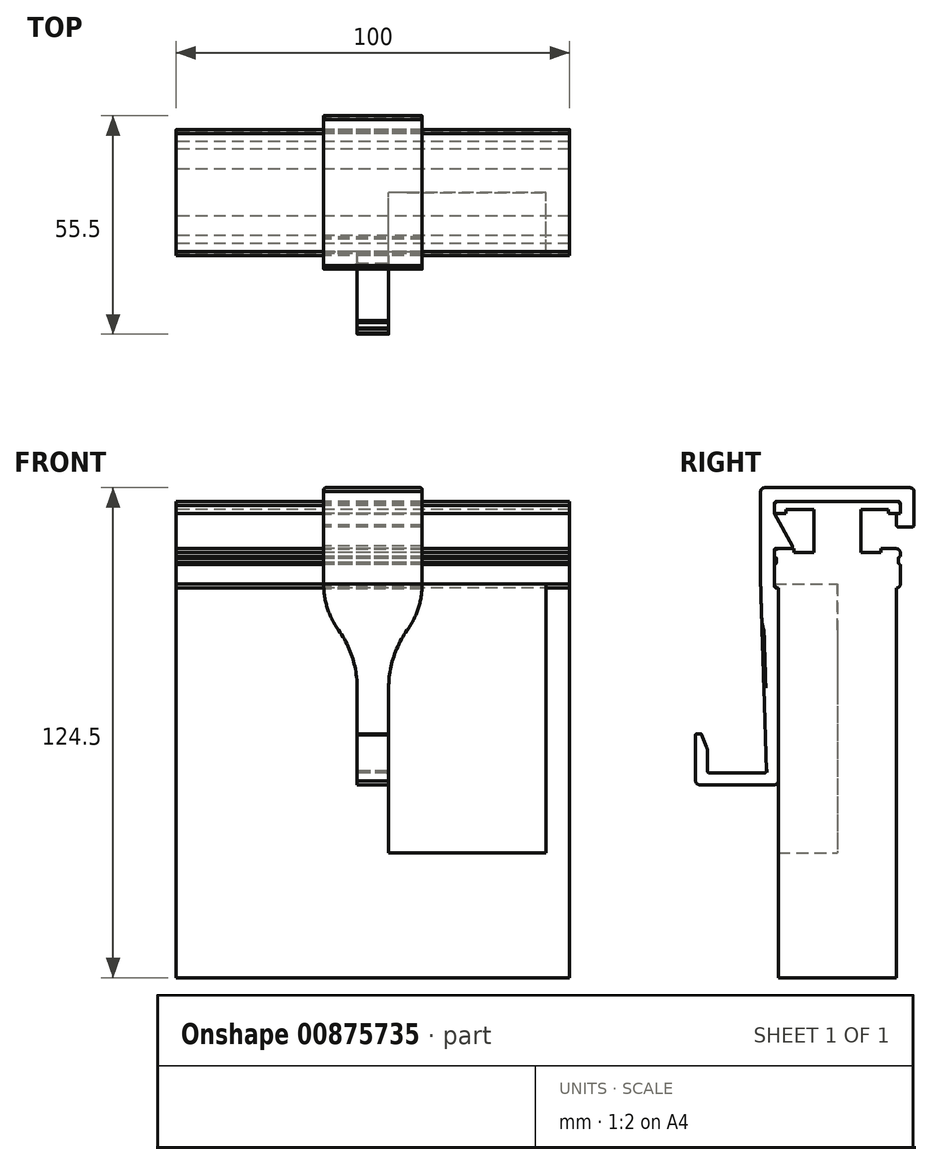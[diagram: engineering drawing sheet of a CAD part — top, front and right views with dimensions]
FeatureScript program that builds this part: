
annotation { "Feature Type Name" : "Feature", "Feature Type Description" : "" }
export const myFeature = defineFeature(function(context is Context, id is Id, definition is map)
    precondition{}
    {
        {
            var Q0;
            Q0=qCreatedBy(makeId("Right.planeOp"),FACE);
            var sketch = newSketch(context, id + "F0", { "sketchPlane" : qUnion([Q0])});
            skLineSegment(sketch, "E0", {"start": v(0, 0) * mm, "end": v(15, 0) * mm});
            skLineSegment(sketch, "E1", {"start": v(16, -1) * mm, "end": v(16, -3) * mm});
            skLineSegment(sketch, "E2", {"start": v(13, -2) * mm, "end": v(6, -2) * mm});
            skLineSegment(sketch, "E3", {"start": v(6, -2) * mm, "end": v(6, -13) * mm});
            skLineSegment(sketch, "E4", {"start": v(6, -13) * mm, "end": v(11, -13) * mm});
            skLineSegment(sketch, "E5", {"start": v(11, -13) * mm, "end": v(11, -12) * mm});
            skLineSegment(sketch, "E6", {"start": v(11, -12) * mm, "end": v(15, -12) * mm});
            skLineSegment(sketch, "E7", {"start": v(16, -13) * mm, "end": v(16, -14) * mm});
            skLineSegment(sketch, "E8", {"start": v(16, -14) * mm, "end": v(16, -14) * mm});
            skLineSegment(sketch, "E9", {"start": v(15.5, -14.5) * mm, "end": v(15.5, -15.5) * mm});
            skLineSegment(sketch, "E10", {"start": v(16, -16) * mm, "end": v(16, -16) * mm});
            skLineSegment(sketch, "E11", {"start": v(16, -16) * mm, "end": v(16, -21) * mm});
            skLineSegment(sketch, "E12", {"start": v(13, -2) * mm, "end": v(13, -3) * mm});
            skLineSegment(sketch, "E13", {"start": v(13, -3) * mm, "end": v(16, -3) * mm});
            skLineSegment(sketch, "E14", {"start": v(15, -22) * mm, "end": v(15, -22) * mm});
            skLineSegment(sketch, "E15", {"start": v(15, -22) * mm, "end": v(15, -21) * mm});
            skLineSegment(sketch, "E16", {"start": v(15, -21) * mm, "end": v(0, -21) * mm});
            skLineSegment(sketch, "E17", {"start": v(0, -21) * mm, "end": v(0, 0) * mm});
            skPoint(sketch, "E18.visualSharp", {"position": v(16, 0) * mm});
            skArc(sketch, "E18.filletArc", {"start": v(16, -1) * mm, "mid": v(15.7, -0.3) * mm, "end": v(15, 0) * mm});
            skPoint(sketch, "E19.visualSharp", {"position": v(16, -12) * mm});
            skArc(sketch, "E19.filletArc", {"start": v(16, -13) * mm, "mid": v(15.7, -12.3) * mm, "end": v(15, -12) * mm});
            skPoint(sketch, "E20.visualSharp", {"position": v(15.5, -14) * mm});
            skArc(sketch, "E20.filletArc", {"start": v(16, -14) * mm, "mid": v(15.65, -14.15) * mm, "end": v(15.5, -14.5) * mm});
            skPoint(sketch, "E21.visualSharp", {"position": v(15.5, -16) * mm});
            skArc(sketch, "E21.filletArc", {"start": v(15.5, -15.5) * mm, "mid": v(15.65, -15.85) * mm, "end": v(16, -16) * mm});
            skPoint(sketch, "E22.visualSharp", {"position": v(16, -22) * mm});
            skArc(sketch, "E22.filletArc", {"start": v(15, -22) * mm, "mid": v(15.7, -21.7) * mm, "end": v(16, -21) * mm});
            skSolve(sketch);
        }
        {
            var Q0;
            Q0 = qSketchRegion(id + "F0", true);
            extrude(context, id + "F1", {"entities" : qUnion([Q0]), "endBound" : BoundingType.SYMMETRIC, "depth" : 100 * mm, "offsetDistance" : 25 * mm});
        }
        {
            var Q0;
            Q0=makeQuery(id+"F1.opExtrude","SWEPT_BODY",BODY,{"disambiguationData":[OSD([sQuery(id+"F0.wireOp",EDGE,"E0"),sQuery(id+"F0.wireOp",EDGE,"E1"),sQuery(id+"F0.wireOp",EDGE,"E2"),sQuery(id+"F0.wireOp",EDGE,"E3"),sQuery(id+"F0.wireOp",EDGE,"E4"),sQuery(id+"F0.wireOp",EDGE,"E5"),sQuery(id+"F0.wireOp",EDGE,"E6"),sQuery(id+"F0.wireOp",EDGE,"E7"),sQuery(id+"F0.wireOp",EDGE,"E9"),sQuery(id+"F0.wireOp",EDGE,"E11"),sQuery(id+"F0.wireOp",EDGE,"E12"),sQuery(id+"F0.wireOp",EDGE,"E13"),sQuery(id+"F0.wireOp",EDGE,"E15"),sQuery(id+"F0.wireOp",EDGE,"E16"),sQuery(id+"F0.wireOp",EDGE,"E17"),sQuery(id+"F0.wireOp",EDGE,"E18.filletArc"),sQuery(id+"F0.wireOp",EDGE,"E19.filletArc"),sQuery(id+"F0.wireOp",EDGE,"E20.filletArc"),sQuery(id+"F0.wireOp",EDGE,"E21.filletArc"),sQuery(id+"F0.wireOp",EDGE,"E22.filletArc")])]});
            var Q1;
            Q1=makeQuery(id+"F1.opExtrude","SWEPT_FACE",FACE,{"disambiguationData":[OSD([sQuery(id+"F0.wireOp",EDGE,"E17")])]});
            mirror(context, id + "F2", {"operationType" : NewBodyOperationType.ADD, "entities" : qUnion([Q0]), "mirrorPlane" : qUnion([Q1])});
        }
        {
            var Q0;
            Q0=qCreatedBy(makeId("Right.planeOp"),FACE);
            var sketch = newSketch(context, id + "F3", { "sketchPlane" : qUnion([Q0])});
            skLineSegment(sketch, "E23.0", {"start": v(15, -21) * mm, "end": v(0, -21) * mm, "construction": true});
            skLineSegment(sketch, "E24.0", {"start": v(15, -22) * mm, "end": v(15, -21) * mm, "construction": true});
            skLineSegment(sketch, "E25.bottom", {"start": v(15, -21) * mm, "end": v(0, -21) * mm});
            skLineSegment(sketch, "E25.top", {"start": v(15, -121) * mm, "end": v(0, -121) * mm});
            skLineSegment(sketch, "E25.left", {"start": v(15, -21) * mm, "end": v(15, -121) * mm});
            skLineSegment(sketch, "E25.right", {"start": v(0, -21) * mm, "end": v(0, -121) * mm});
            skSolve(sketch);
        }
        {
            var Q0;
            Q0 = qSketchRegion(id + "F3", true);
            extrude(context, id + "F4", {"entities" : qUnion([Q0]), "endBound" : BoundingType.SYMMETRIC, "depth" : 100 * mm, "offsetDistance" : 25 * mm});
        }
        {
            var Q0;
            Q0=makeQuery(id+"F4.opExtrude","SWEPT_BODY",BODY,{"disambiguationData":[OSD([sQuery(id+"F3.wireOp",EDGE,"E25.bottom"),sQuery(id+"F3.wireOp",EDGE,"E25.top"),sQuery(id+"F3.wireOp",EDGE,"E25.left"),sQuery(id+"F3.wireOp",EDGE,"E25.right")])]});
            var Q1;
            Q1=makeQuery(id+"F4.opExtrude","SWEPT_FACE",FACE,{"disambiguationData":[OSD([sQuery(id+"F3.wireOp",EDGE,"E25.right")])]});
            mirror(context, id + "F5", {"operationType" : NewBodyOperationType.ADD, "entities" : qUnion([Q0]), "mirrorPlane" : qUnion([Q1])});
        }
        {
            var Q0;
            Q0=qCreatedBy(makeId("Right.planeOp"),FACE);
            var sketch = newSketch(context, id + "F6", { "sketchPlane" : qUnion([Q0])});
            skArc(sketch, "E26.0.0", {"start": v(16, -14) * mm, "mid": v(15.65, -14.15) * mm, "end": v(15.5, -14.5) * mm, "construction": true});
            skLineSegment(sketch, "E26.0.1", {"start": v(15.5, -14.5) * mm, "end": v(15.5, -15.5) * mm, "construction": true});
            skArc(sketch, "E26.0.2", {"start": v(15.5, -15.5) * mm, "mid": v(15.65, -15.85) * mm, "end": v(16, -16) * mm, "construction": true});
            skLineSegment(sketch, "E26.0.3", {"start": v(16, -16) * mm, "end": v(16, -21) * mm, "construction": true});
            skArc(sketch, "E26.0.4", {"start": v(16, -21) * mm, "mid": v(15.7, -21.7) * mm, "end": v(15, -22) * mm, "construction": true});
            skLineSegment(sketch, "E26.0.5", {"start": v(15, -22) * mm, "end": v(15, -21) * mm, "construction": true});
            skLineSegment(sketch, "E26.0.6", {"start": v(15, -21) * mm, "end": v(-15, -21) * mm, "construction": true});
            skLineSegment(sketch, "E26.0.7", {"start": v(-15, -21) * mm, "end": v(-15, -22) * mm, "construction": true});
            skArc(sketch, "E26.0.8", {"start": v(-15, -22) * mm, "mid": v(-15.7, -21.7) * mm, "end": v(-16, -21) * mm, "construction": true});
            skLineSegment(sketch, "E26.0.9", {"start": v(-16, -21) * mm, "end": v(-16, -16) * mm, "construction": true});
            skArc(sketch, "E26.0.10", {"start": v(-16, -16) * mm, "mid": v(-15.65, -15.85) * mm, "end": v(-15.5, -15.5) * mm, "construction": true});
            skLineSegment(sketch, "E26.0.11", {"start": v(-15.5, -15.5) * mm, "end": v(-15.5, -14.5) * mm, "construction": true});
            skArc(sketch, "E26.0.12", {"start": v(-15.5, -14.5) * mm, "mid": v(-15.65, -14.15) * mm, "end": v(-16, -14) * mm, "construction": true});
            skLineSegment(sketch, "E26.0.13", {"start": v(-16, -14) * mm, "end": v(-16, -13) * mm, "construction": true});
            skLineSegment(sketch, "E26.0.15", {"start": v(-15, -12) * mm, "end": v(-11, -12) * mm, "construction": true});
            skLineSegment(sketch, "E26.0.16", {"start": v(-11, -12) * mm, "end": v(-11, -13) * mm, "construction": true});
            skLineSegment(sketch, "E26.0.17", {"start": v(-11, -13) * mm, "end": v(-6, -13) * mm, "construction": true});
            skLineSegment(sketch, "E26.0.18", {"start": v(-6, -13) * mm, "end": v(-6, -2) * mm, "construction": true});
            skLineSegment(sketch, "E26.0.19", {"start": v(-6, -2) * mm, "end": v(-13, -2) * mm, "construction": true});
            skLineSegment(sketch, "E26.0.20", {"start": v(-13, -2) * mm, "end": v(-13, -3) * mm, "construction": true});
            skLineSegment(sketch, "E26.0.21", {"start": v(-13, -3) * mm, "end": v(-16, -3) * mm, "construction": true});
            skArc(sketch, "E26.0.23", {"start": v(-16, -1) * mm, "mid": v(-15.7, -0.3) * mm, "end": v(-15, 0) * mm, "construction": true});
            skLineSegment(sketch, "E26.0.24", {"start": v(-15, 0) * mm, "end": v(15, 0) * mm, "construction": true});
            skArc(sketch, "E26.0.25", {"start": v(15, 0) * mm, "mid": v(15.7, -0.3) * mm, "end": v(16, -1) * mm, "construction": true});
            skLineSegment(sketch, "E26.0.26", {"start": v(16, -1) * mm, "end": v(16, -3) * mm, "construction": true});
            skLineSegment(sketch, "E26.0.27", {"start": v(16, -3) * mm, "end": v(13, -3) * mm, "construction": true});
            skLineSegment(sketch, "E26.0.28", {"start": v(13, -3) * mm, "end": v(13, -2) * mm, "construction": true});
            skLineSegment(sketch, "E26.0.29", {"start": v(13, -2) * mm, "end": v(6, -2) * mm, "construction": true});
            skLineSegment(sketch, "E26.0.30", {"start": v(6, -2) * mm, "end": v(6, -13) * mm, "construction": true});
            skLineSegment(sketch, "E26.0.31", {"start": v(6, -13) * mm, "end": v(11, -13) * mm, "construction": true});
            skLineSegment(sketch, "E26.0.32", {"start": v(11, -13) * mm, "end": v(11, -12) * mm, "construction": true});
            skLineSegment(sketch, "E26.0.33", {"start": v(11, -12) * mm, "end": v(15, -12) * mm, "construction": true});
            skArc(sketch, "E26.0.34", {"start": v(15, -12) * mm, "mid": v(15.7, -12.3) * mm, "end": v(16, -13) * mm, "construction": true});
            skLineSegment(sketch, "E26.0.35", {"start": v(16, -13) * mm, "end": v(16, -14) * mm, "construction": true});
            skLineSegment(sketch, "E27", {"start": v(15, -3.25) * mm, "end": v(15, -6) * mm});
            skLineSegment(sketch, "E28", {"start": v(15.5, -6.5) * mm, "end": v(19, -6.5) * mm});
            skLineSegment(sketch, "E29", {"start": v(19.5, -6) * mm, "end": v(19.5, 2.5) * mm});
            skLineSegment(sketch, "E30", {"start": v(18.5, 3.5) * mm, "end": v(-18.5, 3.5) * mm});
            skLineSegment(sketch, "E31", {"start": v(-19.5, 2.5) * mm, "end": v(-19.5, -21) * mm});
            skLineSegment(sketch, "E32", {"start": v(-16, -21.5) * mm, "end": v(-16, -12.25) * mm});
            skLineSegment(sketch, "E33", {"start": v(-15.5, 0) * mm, "end": v(15.5, 0) * mm});
            skLineSegment(sketch, "E34", {"start": v(16, -0.5) * mm, "end": v(16, -3) * mm});
            skLineSegment(sketch, "E35", {"start": v(16, -3) * mm, "end": v(15.25, -3) * mm});
            skLineSegment(sketch, "E36", {"start": v(-15.25, -22) * mm, "end": v(-15.5, -22) * mm});
            skLineSegment(sketch, "E37", {"start": v(-15, -22.25) * mm, "end": v(-15, -71) * mm});
            skLineSegment(sketch, "E38", {"start": v(-16, -72) * mm, "end": v(-35, -72) * mm});
            skLineSegment(sketch, "E39", {"start": v(-36, -71) * mm, "end": v(-36, -59.25) * mm});
            skLineSegment(sketch, "E40", {"start": v(-35.75, -59) * mm, "end": v(-34.7, -59) * mm});
            skLineSegment(sketch, "E41", {"start": v(-33, -63.5) * mm, "end": v(-33, -68.5) * mm});
            skLineSegment(sketch, "E42", {"start": v(-32.5, -69) * mm, "end": v(-18.52, -69) * mm});
            skLineSegment(sketch, "E43", {"start": v(-19.5, -21) * mm, "end": v(-18.02, -68.48) * mm});
            skPoint(sketch, "E44.visualSharp", {"position": v(-16, -22) * mm});
            skArc(sketch, "E44.filletArc", {"start": v(-16, -21.5) * mm, "mid": v(-15.85, -21.85) * mm, "end": v(-15.5, -22) * mm});
            skPoint(sketch, "E45.visualSharp", {"position": v(-15, -22) * mm});
            skArc(sketch, "E45.filletArc", {"start": v(-15, -22.25) * mm, "mid": v(-15.07, -22.07) * mm, "end": v(-15.25, -22) * mm});
            skPoint(sketch, "E46.visualSharp", {"position": v(-16, 0) * mm});
            skArc(sketch, "E46.filletArc", {"start": v(-15.5, 0) * mm, "mid": v(-15.85, -0.15) * mm, "end": v(-16, -0.5) * mm});
            skPoint(sketch, "E47.visualSharp", {"position": v(16, 0) * mm});
            skArc(sketch, "E47.filletArc", {"start": v(16, -0.5) * mm, "mid": v(15.85, -0.15) * mm, "end": v(15.5, 0) * mm});
            skPoint(sketch, "E48.visualSharp", {"position": v(19.5, 3.5) * mm});
            skArc(sketch, "E48.filletArc", {"start": v(19.5, 2.5) * mm, "mid": v(19.2, 3.2) * mm, "end": v(18.5, 3.5) * mm});
            skPoint(sketch, "E49.visualSharp", {"position": v(-19.5, 3.5) * mm});
            skArc(sketch, "E49.filletArc", {"start": v(-18.5, 3.5) * mm, "mid": v(-19.2, 3.2) * mm, "end": v(-19.5, 2.5) * mm});
            skPoint(sketch, "E50.visualSharp", {"position": v(-33, -69) * mm});
            skArc(sketch, "E50.filletArc", {"start": v(-33, -68.5) * mm, "mid": v(-32.85, -68.85) * mm, "end": v(-32.5, -69) * mm});
            skPoint(sketch, "E51.visualSharp", {"position": v(-36, -72) * mm});
            skArc(sketch, "E51.filletArc", {"start": v(-36, -71) * mm, "mid": v(-35.7, -71.7) * mm, "end": v(-35, -72) * mm});
            skPoint(sketch, "E52.visualSharp", {"position": v(-18, -69) * mm});
            skArc(sketch, "E52.filletArc", {"start": v(-18.52, -69) * mm, "mid": v(-18.16, -68.85) * mm, "end": v(-18.02, -68.48) * mm});
            skPoint(sketch, "E53.visualSharp", {"position": v(-15, -72) * mm});
            skArc(sketch, "E53.filletArc", {"start": v(-16, -72) * mm, "mid": v(-15.3, -71.7) * mm, "end": v(-15, -71) * mm});
            skPoint(sketch, "E54.visualSharp", {"position": v(-36, -59) * mm});
            skArc(sketch, "E54.filletArc", {"start": v(-35.75, -59) * mm, "mid": v(-35.93, -59.07) * mm, "end": v(-36, -59.25) * mm});
            skLineSegment(sketch, "E55", {"start": v(-34.47, -59.16) * mm, "end": v(-33.2, -62.42) * mm});
            skPoint(sketch, "E56.visualSharp", {"position": v(-34.54, -59) * mm});
            skArc(sketch, "E56.filletArc", {"start": v(-34.47, -59.16) * mm, "mid": v(-34.57, -59.04) * mm, "end": v(-34.7, -59) * mm});
            skPoint(sketch, "E57.visualSharp", {"position": v(-33, -62.95) * mm});
            skArc(sketch, "E57.filletArc", {"start": v(-33, -63.5) * mm, "mid": v(-33.05, -62.96) * mm, "end": v(-33.2, -62.42) * mm});
            skLineSegment(sketch, "E58", {"start": v(-11.85, -12) * mm, "end": v(-15.75, -12) * mm});
            skPoint(sketch, "E59.visualSharp", {"position": v(-16, -12) * mm});
            skArc(sketch, "E59.filletArc", {"start": v(-15.75, -12) * mm, "mid": v(-15.93, -12.07) * mm, "end": v(-16, -12.25) * mm});
            skLineSegment(sketch, "E60", {"start": v(-16, -3) * mm, "end": v(-11.41, -11.26) * mm});
            skLineSegment(sketch, "E61", {"start": v(-16, -0.5) * mm, "end": v(-16, -3) * mm});
            skPoint(sketch, "E62.visualSharp", {"position": v(-11, -12) * mm});
            skArc(sketch, "E62.filletArc", {"start": v(-11.85, -12) * mm, "mid": v(-11.42, -11.75) * mm, "end": v(-11.41, -11.26) * mm});
            skPoint(sketch, "E63.visualSharp", {"position": v(15, -6.5) * mm});
            skArc(sketch, "E63.filletArc", {"start": v(15, -6) * mm, "mid": v(15.15, -6.35) * mm, "end": v(15.5, -6.5) * mm});
            skPoint(sketch, "E64.visualSharp", {"position": v(19.5, -6.5) * mm});
            skArc(sketch, "E64.filletArc", {"start": v(19, -6.5) * mm, "mid": v(19.35, -6.35) * mm, "end": v(19.5, -6) * mm});
            skPoint(sketch, "E65.visualSharp", {"position": v(15, -3) * mm});
            skArc(sketch, "E65.filletArc", {"start": v(15.25, -3) * mm, "mid": v(15.07, -3.07) * mm, "end": v(15, -3.25) * mm});
            skSolve(sketch);
        }
        {
            var Q0;
            Q0 = qSketchRegion(id + "F6", true);
            extrude(context, id + "F7", {"entities" : qUnion([Q0]), "depth" : 12.5 * mm, "offsetDistance" : 25 * mm});
        }
        {
            var Q0;
            Q0=qCreatedBy(makeId("Front.planeOp"),FACE);
            var sketch = newSketch(context, id + "F8", { "sketchPlane" : qUnion([Q0])});
            skLineSegment(sketch, "E66.0", {"start": v(12.5, -21) * mm, "end": v(0, -21) * mm, "construction": true});
            skLineSegment(sketch, "E67", {"start": v(0, 0) * mm, "end": v(0, -68.27) * mm, "construction": true});
            skLineSegment(sketch, "E68", {"start": v(3, -21) * mm, "end": v(12.5, -21) * mm});
            skLineSegment(sketch, "E69", {"start": v(44, -21) * mm, "end": v(44, -89.27) * mm});
            skLineSegment(sketch, "E70", {"start": v(44, -89.27) * mm, "end": v(4, -89.27) * mm});
            skArc(sketch, "E71", {"start": v(8.72, -32.7) * mm, "mid": v(5.2, -39.64) * mm, "end": v(4, -47.32) * mm});
            skArc(sketch, "E72", {"start": v(8.72, -32.7) * mm, "mid": v(11.53, -27.15) * mm, "end": v(12.5, -21) * mm});
            skLineSegment(sketch, "E73.trimOffspring", {"start": v(4, -47.32) * mm, "end": v(4, -89.27) * mm});
            skLineSegment(sketch, "E74.trimOffspring", {"start": v(12.5, -21) * mm, "end": v(44, -21) * mm});
            skLineSegment(sketch, "E75.0", {"start": v(12.5, -21) * mm, "end": v(12.5, -68.48) * mm, "construction": true});
            skSolve(sketch);
        }
        {
            var Q0;
            Q0 = qSketchRegion(id + "F8", true);
            extrude(context, id + "F9", {"entities" : qUnion([Q0]), "operationType" : NewBodyOperationType.REMOVE, "depth" : 50 * mm, "offsetDistance" : 25 * mm});
        }
        {
            var Q0;
            Q0=makeQuery(id+"F7.opExtrude","SWEPT_BODY",BODY,{"disambiguationData":[OSD([sQuery(id+"F6.wireOp",EDGE,"E27"),sQuery(id+"F6.wireOp",EDGE,"E28"),sQuery(id+"F6.wireOp",EDGE,"E29"),sQuery(id+"F6.wireOp",EDGE,"E30"),sQuery(id+"F6.wireOp",EDGE,"E31"),sQuery(id+"F6.wireOp",EDGE,"E32"),sQuery(id+"F6.wireOp",EDGE,"E33"),sQuery(id+"F6.wireOp",EDGE,"E34"),sQuery(id+"F6.wireOp",EDGE,"E35"),sQuery(id+"F6.wireOp",EDGE,"E36"),sQuery(id+"F6.wireOp",EDGE,"E37"),sQuery(id+"F6.wireOp",EDGE,"E38"),sQuery(id+"F6.wireOp",EDGE,"E39"),sQuery(id+"F6.wireOp",EDGE,"E40"),sQuery(id+"F6.wireOp",EDGE,"E41"),sQuery(id+"F6.wireOp",EDGE,"E42"),sQuery(id+"F6.wireOp",EDGE,"E43"),sQuery(id+"F6.wireOp",EDGE,"E44.filletArc"),sQuery(id+"F6.wireOp",EDGE,"E45.filletArc"),sQuery(id+"F6.wireOp",EDGE,"E46.filletArc"),sQuery(id+"F6.wireOp",EDGE,"E47.filletArc"),sQuery(id+"F6.wireOp",EDGE,"E48.filletArc"),sQuery(id+"F6.wireOp",EDGE,"E49.filletArc"),sQuery(id+"F6.wireOp",EDGE,"E50.filletArc"),sQuery(id+"F6.wireOp",EDGE,"E51.filletArc"),sQuery(id+"F6.wireOp",EDGE,"E52.filletArc"),sQuery(id+"F6.wireOp",EDGE,"E53.filletArc"),sQuery(id+"F6.wireOp",EDGE,"E54.filletArc"),sQuery(id+"F6.wireOp",EDGE,"E55"),sQuery(id+"F6.wireOp",EDGE,"E56.filletArc"),sQuery(id+"F6.wireOp",EDGE,"E57.filletArc")])]});
            var Q1;
            Q1=makeQuery(id+"F7.opExtrude","CAP_FACE",FACE,{"disambiguationData":[OSD([sQuery(id+"F6.wireOp",EDGE,"E27"),sQuery(id+"F6.wireOp",EDGE,"E28"),sQuery(id+"F6.wireOp",EDGE,"E29"),sQuery(id+"F6.wireOp",EDGE,"E30"),sQuery(id+"F6.wireOp",EDGE,"E31"),sQuery(id+"F6.wireOp",EDGE,"E32"),sQuery(id+"F6.wireOp",EDGE,"E33"),sQuery(id+"F6.wireOp",EDGE,"E34"),sQuery(id+"F6.wireOp",EDGE,"E35"),sQuery(id+"F6.wireOp",EDGE,"E36"),sQuery(id+"F6.wireOp",EDGE,"E37"),sQuery(id+"F6.wireOp",EDGE,"E38"),sQuery(id+"F6.wireOp",EDGE,"E39"),sQuery(id+"F6.wireOp",EDGE,"E40"),sQuery(id+"F6.wireOp",EDGE,"E41"),sQuery(id+"F6.wireOp",EDGE,"E42"),sQuery(id+"F6.wireOp",EDGE,"E43"),sQuery(id+"F6.wireOp",EDGE,"E44.filletArc"),sQuery(id+"F6.wireOp",EDGE,"E45.filletArc"),sQuery(id+"F6.wireOp",EDGE,"E46.filletArc"),sQuery(id+"F6.wireOp",EDGE,"E47.filletArc"),sQuery(id+"F6.wireOp",EDGE,"E48.filletArc"),sQuery(id+"F6.wireOp",EDGE,"E49.filletArc"),sQuery(id+"F6.wireOp",EDGE,"E50.filletArc"),sQuery(id+"F6.wireOp",EDGE,"E51.filletArc"),sQuery(id+"F6.wireOp",EDGE,"E52.filletArc"),sQuery(id+"F6.wireOp",EDGE,"E53.filletArc"),sQuery(id+"F6.wireOp",EDGE,"E54.filletArc"),sQuery(id+"F6.wireOp",EDGE,"E55"),sQuery(id+"F6.wireOp",EDGE,"E56.filletArc"),sQuery(id+"F6.wireOp",EDGE,"E57.filletArc")])],"isStart":true});
            mirror(context, id + "F10", {"operationType" : NewBodyOperationType.ADD, "entities" : qUnion([Q0]), "mirrorPlane" : qUnion([Q1])});
        }
        {
            var Q0;
            Q0=makeQuery(id+"F10.opPattern","COPY",EDGE,{"derivedFrom":makeQuery(id+"F7.opExtrude","CAP_EDGE",EDGE,{"disambiguationData":[OSD([sQuery(id+"F6.wireOp",EDGE,"E30")])],"isStart":false}),"instanceName":"1"});
            var Q1;
            Q1=makeQuery(id+"F7.opExtrude","CAP_EDGE",EDGE,{"disambiguationData":[OSD([sQuery(id+"F6.wireOp",EDGE,"E30")])],"isStart":false});
            fillet(context, id + "F11", {"entities" : qUnion([Q0, Q1]), "radius" : .5 * mm, "tangentPropagation" : true, "allowEdgeOverflow" : false});
        }
        {
            var Q0;
            Q0=makeQuery(id+"F10.opPattern","COPY",EDGE,{"derivedFrom":makeQuery(id+"F9.boolean.opBoolean","INTERSECT",EDGE,{"derivedFrom":[makeQuery(id+"F7.opExtrude","SWEPT_FACE",FACE,{"disambiguationData":[OSD([sQuery(id+"F6.wireOp",EDGE,"E43")])]}),makeQuery(id+"F9.opExtrude","SWEPT_FACE",FACE,{"disambiguationData":[OSD([sQuery(id+"F8.wireOp",EDGE,"E73.trimOffspring")])]})]}),"instanceName":"1"});
            var Q1;
            Q1=makeQuery(id+"F9.boolean.opBoolean","INTERSECT",EDGE,{"derivedFrom":[makeQuery(id+"F7.opExtrude","SWEPT_FACE",FACE,{"disambiguationData":[OSD([sQuery(id+"F6.wireOp",EDGE,"E43")])]}),makeQuery(id+"F9.opExtrude","SWEPT_FACE",FACE,{"disambiguationData":[OSD([sQuery(id+"F8.wireOp",EDGE,"E73.trimOffspring")])]})]});
            fillet(context, id + "F12", {"entities" : qUnion([Q0, Q1]), "radius" : .5 * mm, "tangentPropagation" : true, "allowEdgeOverflow" : false});
        }
    });
